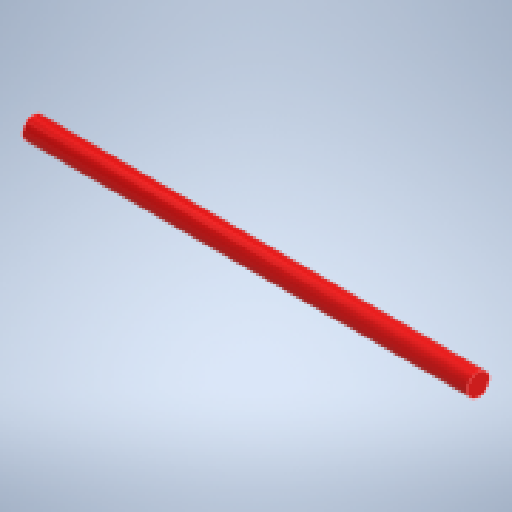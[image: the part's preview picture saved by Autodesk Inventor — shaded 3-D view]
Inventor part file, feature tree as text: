
AUTODESK INVENTOR PART (.ipt)
format: ipt  version: 2025.2 (Build 292293000, 293)  size: 158,720 bytes
history: native  units: mm
features: sketch x4, extrude x2, revolve x2, other x1
ambient origin geometry x8: Origin, YZ Plane, XZ Plane, XY Plane, X Axis, Y Axis, Z Axis, Center Point
bodies: Body1 (feature_tree)
feature tree (9):
  other  "ソリッド1"
  extrude  "押し出し1"  Depth=0.5mm
  revolve  "回転1"
  extrude  "押し出し2"  Depth=1.0mm TaperAngle=0.0deg
  revolve  "回転2"
  sketch  "スケッチ1"
  sketch  "スケッチ2"
  sketch  "スケッチ3"
  sketch  "スケッチ4"
